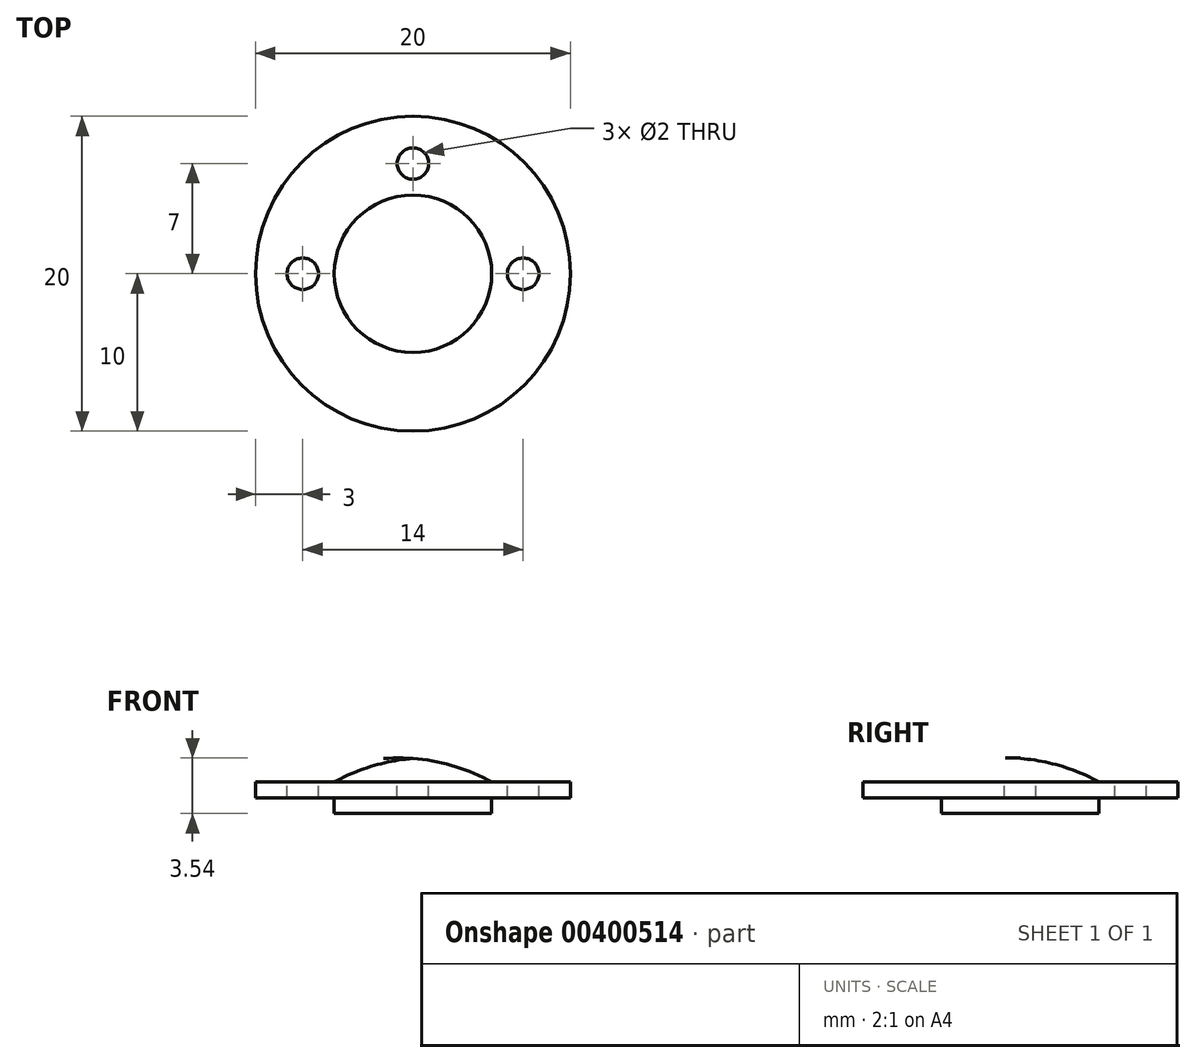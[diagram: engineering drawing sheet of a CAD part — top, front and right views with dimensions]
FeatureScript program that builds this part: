
annotation { "Feature Type Name" : "Feature", "Feature Type Description" : "" }
export const myFeature = defineFeature(function(context is Context, id is Id, definition is map)
    precondition{}
    {
        {
            var Q0;
            Q0=qCreatedBy(makeId("Right.planeOp"),FACE);
            var sketch = newSketch(context, id + "F0", { "sketchPlane" : qUnion([Q0])});
            skLineSegment(sketch, "E0", {"start": v(0, 0) * mm, "end": v(-5, 0) * mm});
            skLineSegment(sketch, "E1", {"start": v(-5, 0) * mm, "end": v(-5, 1) * mm});
            skLineSegment(sketch, "E2", {"start": v(-5, 1) * mm, "end": v(-10, 1) * mm});
            skLineSegment(sketch, "E3", {"start": v(-10, 1) * mm, "end": v(-10, 2) * mm});
            skLineSegment(sketch, "E4", {"start": v(-10, 2) * mm, "end": v(-5, 2) * mm});
            skArc(sketch, "E5", {"start": v(0, 3.5) * mm, "mid": v(-2.58, 3.02) * mm, "end": v(-5, 2) * mm});
            skLineSegment(sketch, "E6", {"start": v(0, 0) * mm, "end": v(0, 3.5) * mm});
            skSolve(sketch);
        }
        {
            var Q0;
            Q0=makeQuery(id+"F0.imprint","IMPRINT",FACE,{"disambiguationData":[TD([[makeQuery(id+"F0.imprint","IMPRINT",EDGE,{"derivedFrom":sQuery(id+"F0.wireOp",EDGE,"E0")}),-1.0]])]});
            var Q1;
            Q1=sQuery(id+"F0.wireOp",EDGE,"E6");
            revolve(context, id + "F1", {"entities" : qUnion([Q0]), "axis" : qUnion([Q1]), "revolveType" : RevolveType.FULL});
        }
        {
            var Q0;
            Q0=makeQuery(id+"F1.opRevolve","SWEPT_FACE",FACE,{"disambiguationData":[OSD([sQuery(id+"F0.wireOp",EDGE,"E4")])]});
            var sketch = newSketch(context, id + "F2", { "sketchPlane" : qUnion([Q0])});
            skCircle(sketch, "E7", {"center": v(0, 7) * mm, "radius": 1 * mm});
            skCircle(sketch, "E8", {"center": v(-7, 0) * mm, "radius": 1 * mm});
            skCircle(sketch, "E9", {"center": v(7, 0) * mm, "radius": 1 * mm});
            skSolve(sketch);
        }
        {
            var Q0;
            Q0 = qSketchRegion(id + "F2", true);
            extrude(context, id + "F3", {"entities" : qUnion([Q0]), "operationType" : NewBodyOperationType.REMOVE, "oppositeDirection" : true, "depth" : 5 * mm});
        }
    });
